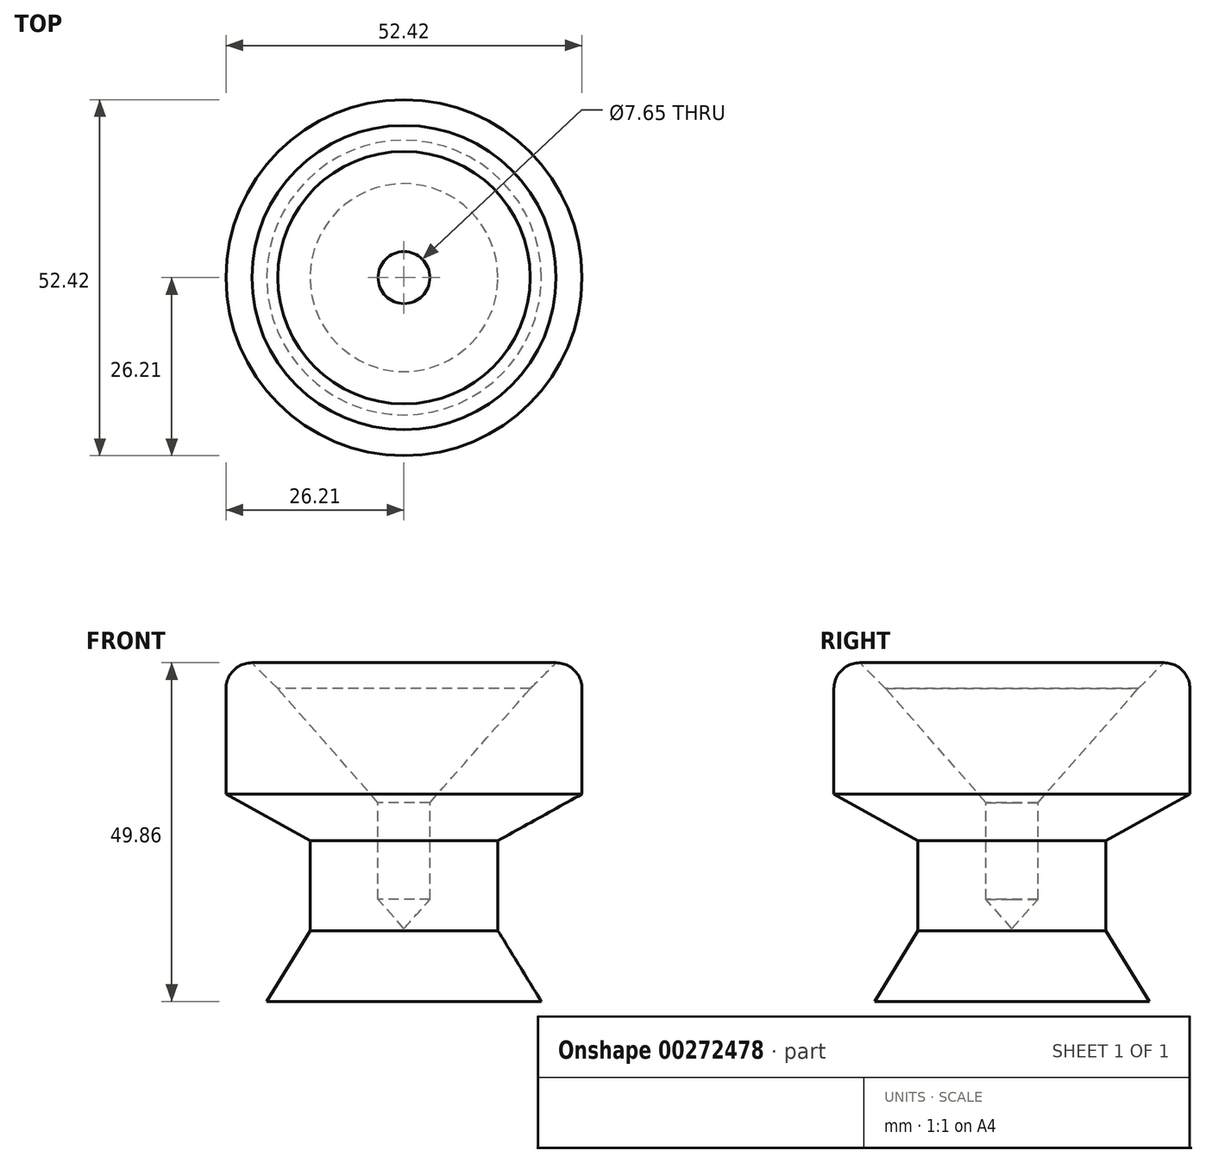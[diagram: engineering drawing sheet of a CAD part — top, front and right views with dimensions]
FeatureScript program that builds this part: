
annotation { "Feature Type Name" : "Feature", "Feature Type Description" : "" }
export const myFeature = defineFeature(function(context is Context, id is Id, definition is map)
    precondition{}
    {
        {
            var Q0;
            Q0=qCreatedBy(makeId("Front.planeOp"),FACE);
            var sketch = newSketch(context, id + "F0", { "sketchPlane" : qUnion([Q0])});
            skLineSegment(sketch, "E0.bottom", {"start": v(0, 11.04) * mm, "end": v(22.4, 11.04) * mm});
            skLineSegment(sketch, "E0.top", {"start": v(0, -38.82) * mm, "end": v(20.22, -38.82) * mm});
            skLineSegment(sketch, "E0.left", {"start": v(0, 11.04) * mm, "end": v(0, -38.82) * mm});
            skLineSegment(sketch, "E0.right", {"start": v(26.21, 7.23) * mm, "end": v(26.21, -32.83) * mm});
            skPoint(sketch, "E1.visualSharp", {"position": v(26.21, 11.04) * mm});
            skArc(sketch, "E1.filletArc", {"start": v(26.21, 7.23) * mm, "mid": v(25.1, 9.92) * mm, "end": v(22.4, 11.04) * mm});
            skPoint(sketch, "E2.visualSharp", {"position": v(26.21, -38.82) * mm});
            skArc(sketch, "E2.filletArc", {"start": v(20.22, -38.82) * mm, "mid": v(24.46, -37.07) * mm, "end": v(26.21, -32.83) * mm});
            skLineSegment(sketch, "E3.bottom", {"start": v(0, 7.23) * mm, "end": v(18.6, 7.23) * mm});
            skLineSegment(sketch, "E3.top", {"start": v(0, -35.01) * mm, "end": v(18.6, -35.01) * mm});
            skLineSegment(sketch, "E3.left", {"start": v(0, 7.23) * mm, "end": v(0, -35.01) * mm});
            skLineSegment(sketch, "E3.right", {"start": v(18.6, 7.23) * mm, "end": v(18.6, -35.01) * mm});
            skLineSegment(sketch, "E4", {"start": v(22.4, 11.04) * mm, "end": v(18.6, 7.23) * mm});
            skLineSegment(sketch, "E5", {"start": v(26.21, -8.3) * mm, "end": v(13.83, -15.16) * mm});
            skLineSegment(sketch, "E6", {"start": v(13.83, -15.16) * mm, "end": v(13.83, -28.43) * mm});
            skLineSegment(sketch, "E7", {"start": v(13.83, -28.43) * mm, "end": v(20.22, -38.82) * mm});
            skLineSegment(sketch, "E8", {"start": v(18.6, 7.23) * mm, "end": v(0, -13.9) * mm});
            skLineSegment(sketch, "E9", {"start": v(3.82, -9.55) * mm, "end": v(3.82, -23.78) * mm});
            skLineSegment(sketch, "E10", {"start": v(3.82, -23.78) * mm, "end": v(0, -28.13) * mm});
            skSolve(sketch);
        }
        {
            var Q0;
            {var subQ1=sQuery(id+"F0.wireOp",EDGE,"E0.top");Q0=makeQuery(id+"F0.imprint","IMPRINT",FACE,{"disambiguationData":[TD([[makeQuery(id+"F0.imprint","IMPRINT",EDGE,{"derivedFrom":subQ1}),1.0]])]});}
            var Q1;
            {var subQ4=sQuery(id+"F0.wireOp",EDGE,"E1.filletArc");Q1=makeQuery(id+"F0.imprint","IMPRINT",FACE,{"disambiguationData":[TD([[makeQuery(id+"F0.imprint","IMPRINT",EDGE,{"derivedFrom":subQ4}),1.0]])]});}
            var Q2;
            {var subQ0=sQuery(id+"F0.wireOp",EDGE,"E6");Q2=makeQuery(id+"F0.imprint","IMPRINT",FACE,{"disambiguationData":[TD([[makeQuery(id+"F0.imprint","IMPRINT",EDGE,{"derivedFrom":subQ0}),-1.0]])]});}
            var Q3;
            Q3=sQuery(id+"F0.wireOp",EDGE,"E0.left");
            revolve(context, id + "F1", {"entities" : qUnion([Q0, Q1, Q2]), "axis" : qUnion([Q3]), "revolveType" : RevolveType.FULL});
        }
    });
